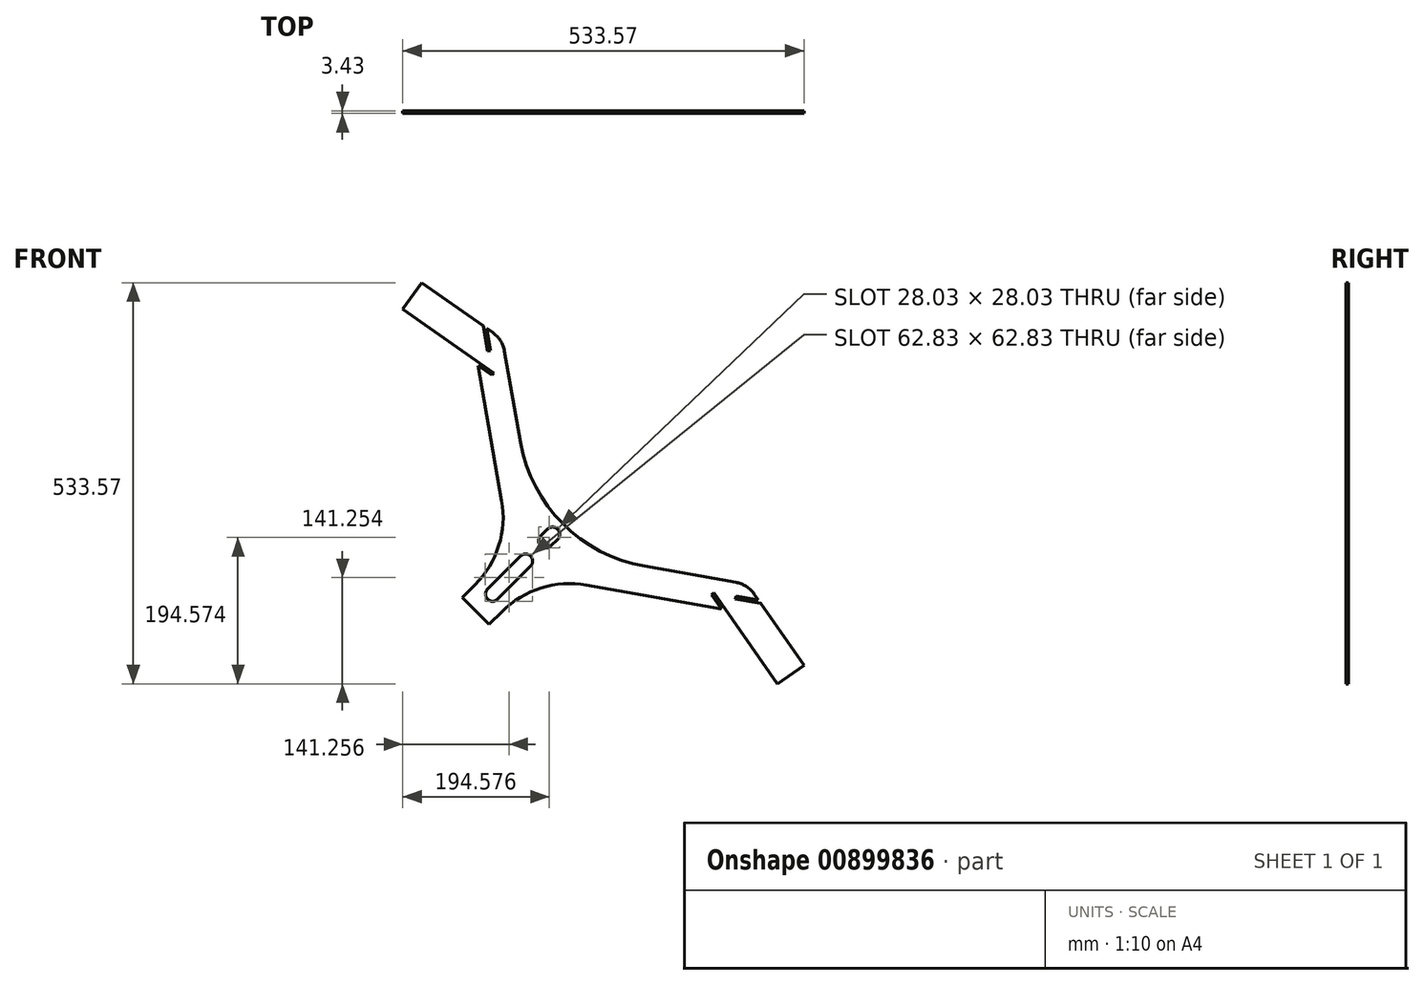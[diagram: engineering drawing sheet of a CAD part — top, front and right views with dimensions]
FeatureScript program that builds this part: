
annotation { "Feature Type Name" : "Feature", "Feature Type Description" : "" }
export const myFeature = defineFeature(function(context is Context, id is Id, definition is map)
    precondition{}
    {
        {
            var Q0;
            Q0=qCreatedBy(makeId("Front.planeOp"),FACE);
            var sketch = newSketch(context, id + "F0", { "sketchPlane" : qUnion([Q0])});
            skLineSegment(sketch, "E0", {"start": v(-198.21, -327.62) * mm, "end": v(-198.88, -331.37) * mm});
            skLineSegment(sketch, "E1", {"start": v(-198.88, -331.37) * mm, "end": v(-165.36, -337.28) * mm});
            skLineSegment(sketch, "E2", {"start": v(-107.74, -419.57) * mm, "end": v(-165.36, -337.28) * mm});
            skLineSegment(sketch, "E3", {"start": v(-143.1, -444.34) * mm, "end": v(-107.74, -419.57) * mm});
            skLineSegment(sketch, "E4", {"start": v(-227.76, -323.44) * mm, "end": v(-143.1, -444.34) * mm});
            skLineSegment(sketch, "E5", {"start": v(-227.76, -323.44) * mm, "end": v(-230.88, -325.63) * mm});
            skLineSegment(sketch, "E6", {"start": v(-230.88, -325.63) * mm, "end": v(-217.61, -344.57) * mm});
            skLineSegment(sketch, "E7", {"start": v(-397.34, -312.88) * mm, "end": v(-217.61, -344.57) * mm});
            skArc(sketch, "E8", {"start": v(-397.34, -312.88) * mm, "mid": v(-457.58, -316.83) * mm, "end": v(-509.2, -348.15) * mm});
            skLineSegment(sketch, "E9", {"start": v(-526.43, -365.39) * mm, "end": v(-509.2, -348.15) * mm});
            skLineSegment(sketch, "E10", {"start": v(-562.35, -329.47) * mm, "end": v(-526.43, -365.39) * mm});
            skLineSegment(sketch, "E11", {"start": v(-545.12, -312.23) * mm, "end": v(-562.35, -329.47) * mm});
            skArc(sketch, "E12", {"start": v(-545.12, -312.23) * mm, "mid": v(-513.8, -260.62) * mm, "end": v(-509.85, -200.37) * mm});
            skLineSegment(sketch, "E13", {"start": v(-541.54, -20.65) * mm, "end": v(-522.6, -33.91) * mm});
            skLineSegment(sketch, "E14", {"start": v(-522.6, -33.91) * mm, "end": v(-520.4, -30.8) * mm});
            skLineSegment(sketch, "E15", {"start": v(-641.3, 53.86) * mm, "end": v(-520.4, -30.8) * mm});
            skLineSegment(sketch, "E16", {"start": v(-616.54, 89.23) * mm, "end": v(-641.3, 53.86) * mm});
            skLineSegment(sketch, "E17", {"start": v(-534.25, 31.61) * mm, "end": v(-616.54, 89.23) * mm});
            skLineSegment(sketch, "E18", {"start": v(-534.25, 31.61) * mm, "end": v(-528.34, -1.9) * mm});
            skLineSegment(sketch, "E19", {"start": v(-528.34, -1.9) * mm, "end": v(-524.59, -1.25) * mm});
            skLineSegment(sketch, "E20", {"start": v(-524.59, -1.25) * mm, "end": v(-529.84, 28.52) * mm});
            skLineSegment(sketch, "E21", {"start": v(-521.87, 22.94) * mm, "end": v(-529.84, 28.52) * mm});
            skArc(sketch, "E22", {"start": v(-506.2, -1.65) * mm, "mid": v(-511.6, 12.2) * mm, "end": v(-521.87, 22.94) * mm});
            skLineSegment(sketch, "E23", {"start": v(-484.8, -123) * mm, "end": v(-506.2, -1.65) * mm});
            skArc(sketch, "E24", {"start": v(-484.8, -123) * mm, "mid": v(-428.38, -231.4) * mm, "end": v(-319.98, -287.84) * mm});
            skLineSegment(sketch, "E25", {"start": v(-198.62, -309.24) * mm, "end": v(-319.98, -287.84) * mm});
            skArc(sketch, "E26", {"start": v(-174.02, -324.9) * mm, "mid": v(-184.76, -314.62) * mm, "end": v(-198.62, -309.24) * mm});
            skLineSegment(sketch, "E27", {"start": v(-168.45, -332.87) * mm, "end": v(-174.02, -324.9) * mm});
            skLineSegment(sketch, "E28", {"start": v(-168.45, -332.87) * mm, "end": v(-198.21, -327.62) * mm});
            skLineSegment(sketch, "E29", {"start": v(-471.43, -287.93) * mm, "end": v(-515.2, -331.71) * mm});
            skArc(sketch, "E30", {"start": v(-471.43, -287.93) * mm, "mid": v(-471.43, -274.46) * mm, "end": v(-484.9, -274.46) * mm});
            skLineSegment(sketch, "E31", {"start": v(-528.68, -318.24) * mm, "end": v(-484.9, -274.46) * mm});
            skArc(sketch, "E32", {"start": v(-528.68, -318.24) * mm, "mid": v(-528.68, -331.71) * mm, "end": v(-515.2, -331.71) * mm});
            skLineSegment(sketch, "E33", {"start": v(-435.5, -252.01) * mm, "end": v(-444.49, -261) * mm});
            skArc(sketch, "E34", {"start": v(-435.5, -252.01) * mm, "mid": v(-435.5, -238.54) * mm, "end": v(-448.98, -238.54) * mm});
            skLineSegment(sketch, "E35", {"start": v(-457.96, -247.52) * mm, "end": v(-448.98, -238.54) * mm});
            skArc(sketch, "E36", {"start": v(-457.96, -247.52) * mm, "mid": v(-457.96, -261) * mm, "end": v(-444.49, -261) * mm});
            skLineSegment(sketch, "E37", {"start": v(-541.54, -20.65) * mm, "end": v(-509.85, -200.37) * mm});
            skSolve(sketch);
        }
        {
            var Q0;
            Q0 = qSketchRegion(id + "F0", true);
            extrude(context, id + "F1", {"entities" : qUnion([Q0]), "depth" : 3.43 * mm, "offsetDistance" : 25.4 * mm});
        }
    });
